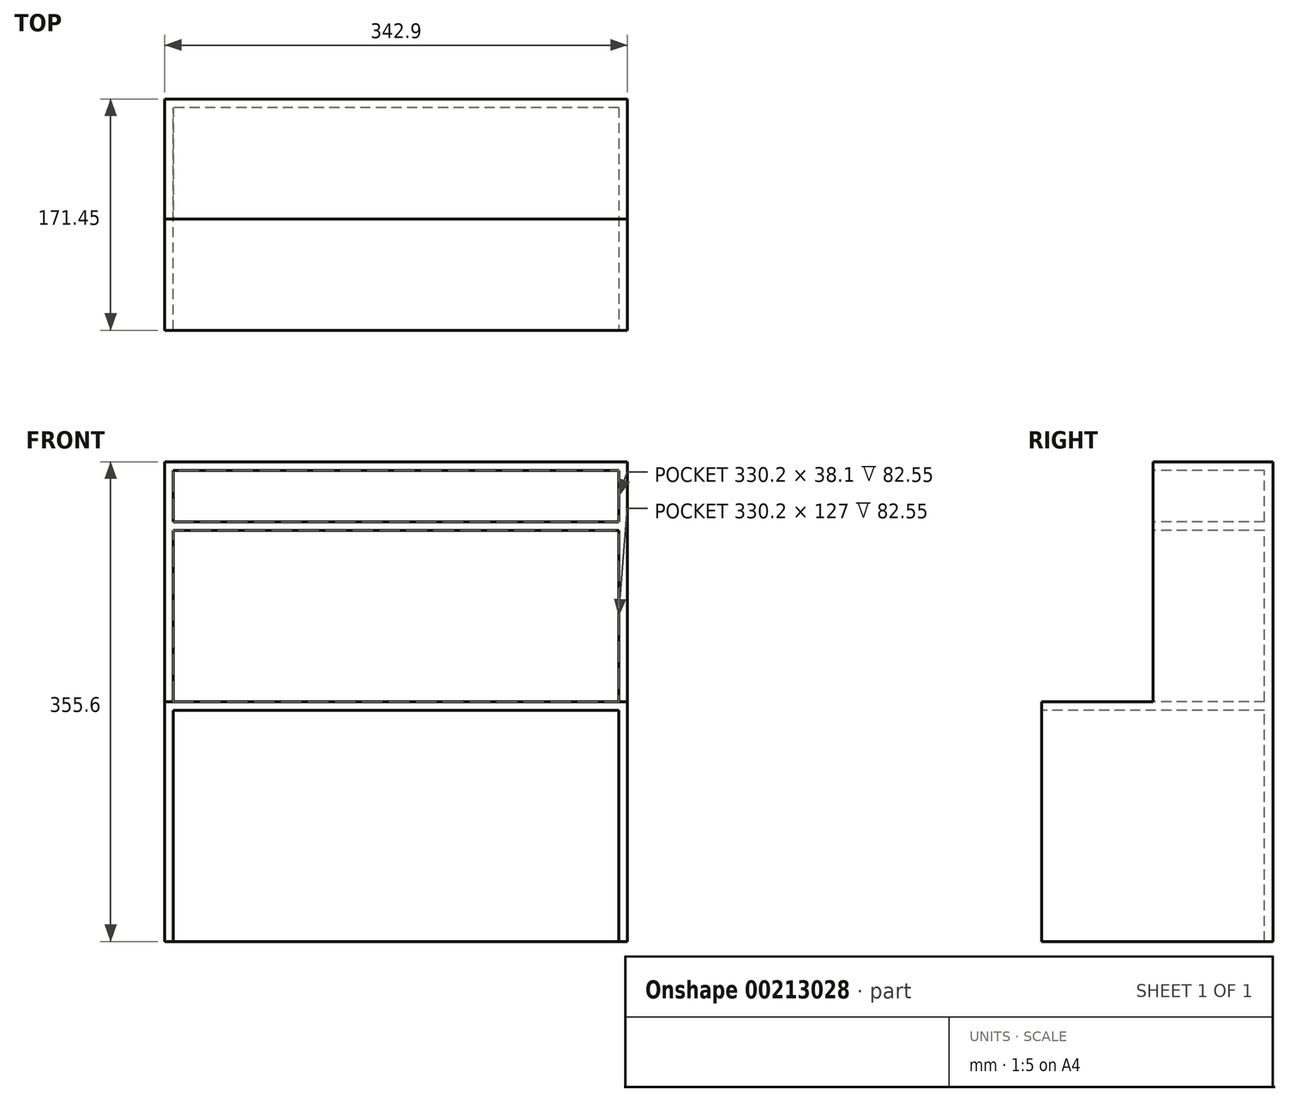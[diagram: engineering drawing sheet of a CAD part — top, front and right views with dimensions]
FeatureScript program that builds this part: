
annotation { "Feature Type Name" : "Feature", "Feature Type Description" : "" }
export const myFeature = defineFeature(function(context is Context, id is Id, definition is map)
    precondition{}
    {
        {
            var Q0;
            Q0=qCreatedBy(makeId("Right.planeOp"),FACE);
            cPlane(context, id + "F0", {"entities" : qUnion([Q0]), "cplaneType" : CPlaneType.OFFSET, "offset" : 165.1 * mm, "width" : 152.4 * mm, "height" : 152.4 * mm});
        }
        {
            var Q0;
            Q0=qCreatedBy(id+"F0.planeOp",FACE);
            var sketch = newSketch(context, id + "F1", { "sketchPlane" : qUnion([Q0])});
            skLineSegment(sketch, "E0.bottom", {"start": v(-82.55, 0) * mm, "end": v(82.55, 0) * mm});
            skLineSegment(sketch, "E0.top", {"start": v(-82.55, 177.8) * mm, "end": v(0, 177.8) * mm});
            skLineSegment(sketch, "E0.left", {"start": v(-82.55, 0) * mm, "end": v(-82.55, 177.8) * mm});
            skLineSegment(sketch, "E1", {"start": v(-82.55, 88.9) * mm, "end": v(0, 88.9) * mm, "construction": true});
            skLineSegment(sketch, "E2", {"start": v(0, 177.8) * mm, "end": v(0, 355.6) * mm});
            skPoint(sketch, "E2.endSnap0", {"position": v(0, 177.8) * mm});
            skLineSegment(sketch, "E3", {"start": v(0, 355.6) * mm, "end": v(82.55, 355.6) * mm});
            skLineSegment(sketch, "E4", {"start": v(82.55, 0) * mm, "end": v(82.55, 355.6) * mm});
            skLineSegment(sketch, "E5", {"start": v(0, 88.9) * mm, "end": v(82.55, 88.9) * mm, "construction": true});
            skSolve(sketch);
        }
        {
            var Q0;
            Q0=makeQuery(id+"F1.imprint","IMPRINT",FACE,{"disambiguationData":[TD([[makeQuery(id+"F1.imprint","IMPRINT",EDGE,{"derivedFrom":sQuery(id+"F1.wireOp",EDGE,"E0.bottom")}),1.0]])]});
            extrude(context, id + "F2", {"entities" : qUnion([Q0]), "depth" : 6.35 * mm});
        }
        {
            var Q0;
            Q0=makeQuery(id+"F2.opExtrude","SWEPT_FACE",FACE,{"disambiguationData":[OSD([sQuery(id+"F1.wireOp",EDGE,"E0.left")])]});
            var sketch = newSketch(context, id + "F3", { "sketchPlane" : qUnion([Q0])});
            skLineSegment(sketch, "E6.bottom", {"start": v(165.1, 177.8) * mm, "end": v(0, 177.8) * mm});
            skLineSegment(sketch, "E6.top", {"start": v(165.1, 171.45) * mm, "end": v(0, 171.45) * mm});
            skLineSegment(sketch, "E6.left", {"start": v(165.1, 177.8) * mm, "end": v(165.1, 171.45) * mm});
            skLineSegment(sketch, "E6.right", {"start": v(0, 177.8) * mm, "end": v(0, 171.45) * mm});
            skSolve(sketch);
        }
        {
            var Q0;
            Q0=makeQuery(id+"F3.imprint","IMPRINT",FACE,{"disambiguationData":[TD([[makeQuery(id+"F3.imprint","IMPRINT",EDGE,{"derivedFrom":sQuery(id+"F3.wireOp",EDGE,"E6.bottom")}),1.0]])]});
            var Q1;
            Q1=makeQuery(id+"F2.opExtrude","SWEPT_FACE",FACE,{"disambiguationData":[OSD([sQuery(id+"F1.wireOp",EDGE,"E4")])]});
            extrude(context, id + "F4", {"entities" : qUnion([Q0]), "operationType" : NewBodyOperationType.ADD, "endBound" : BoundingType.UP_TO_SURFACE, "oppositeDirection" : true, "endBoundEntityFace" : qUnion([Q1]), "depth" : 25.4 * mm});
        }
        {
            var Q0;
            Q0=makeQuery(id+"F2.opExtrude","SWEPT_FACE",FACE,{"disambiguationData":[OSD([sQuery(id+"F1.wireOp",EDGE,"E2")])]});
            var sketch = newSketch(context, id + "F5", { "sketchPlane" : qUnion([Q0])});
            skLineSegment(sketch, "E7.bottom", {"start": v(165.1, 355.6) * mm, "end": v(0, 355.6) * mm});
            skLineSegment(sketch, "E7.top", {"start": v(165.1, 349.25) * mm, "end": v(0, 349.25) * mm});
            skLineSegment(sketch, "E7.left", {"start": v(165.1, 355.6) * mm, "end": v(165.1, 349.25) * mm});
            skLineSegment(sketch, "E7.right", {"start": v(0, 355.6) * mm, "end": v(0, 349.25) * mm});
            skLineSegment(sketch, "E8.bottom", {"start": v(165.1, 311.15) * mm, "end": v(0, 311.15) * mm});
            skLineSegment(sketch, "E8.top", {"start": v(165.1, 304.8) * mm, "end": v(0, 304.8) * mm});
            skLineSegment(sketch, "E8.left", {"start": v(165.1, 311.15) * mm, "end": v(165.1, 304.8) * mm});
            skLineSegment(sketch, "E8.right", {"start": v(0, 311.15) * mm, "end": v(0, 304.8) * mm});
            skSolve(sketch);
        }
        {
            var Q0;
            Q0=makeQuery(id+"F5.imprint","IMPRINT",FACE,{"disambiguationData":[TD([[makeQuery(id+"F5.imprint","IMPRINT",EDGE,{"derivedFrom":sQuery(id+"F5.wireOp",EDGE,"E7.bottom")}),1.0]])]});
            var Q1;
            Q1=makeQuery(id+"F5.imprint","IMPRINT",FACE,{"disambiguationData":[TD([[makeQuery(id+"F5.imprint","IMPRINT",EDGE,{"derivedFrom":sQuery(id+"F5.wireOp",EDGE,"E8.bottom")}),1.0]])]});
            var Q2;
            {var subQ0=sQuery(id+"F1.wireOp",EDGE,"E4");Q2=makeQuery(id+"F4.boolean.opBoolean","MERGE",FACE,{"derivedFrom":[makeQuery(id+"F2.opExtrude","SWEPT_FACE",FACE,{"disambiguationData":[OSD([subQ0])]}),makeQuery(id+"F4.opExtrude","CAP_FACE",FACE,{"disambiguationData":[OSD([subQ0])],"isStart":false})]});}
            extrude(context, id + "F6", {"entities" : qUnion([Q0, Q1]), "operationType" : NewBodyOperationType.ADD, "endBound" : BoundingType.UP_TO_SURFACE, "oppositeDirection" : true, "endBoundEntityFace" : qUnion([Q2]), "depth" : 25.4 * mm});
        }
        {
            var Q0;
            Q0=makeQuery(id+"F2.opExtrude","SWEPT_BODY",BODY,{"disambiguationData":[OSD([sQuery(id+"F1.wireOp",EDGE,"E0.bottom"),sQuery(id+"F1.wireOp",EDGE,"E0.top"),sQuery(id+"F1.wireOp",EDGE,"E0.left"),sQuery(id+"F1.wireOp",EDGE,"E2"),sQuery(id+"F1.wireOp",EDGE,"E3"),sQuery(id+"F1.wireOp",EDGE,"E4")])]});
            var Q1;
            Q1=qCreatedBy(makeId("Right.planeOp"),FACE);
            mirror(context, id + "F7", {"operationType" : NewBodyOperationType.ADD, "entities" : qUnion([Q0]), "mirrorPlane" : qUnion([Q1])});
        }
        {
            var Q0;
            {var subQ0=sQuery(id+"F1.wireOp",EDGE,"E4");var subQ1=makeQuery(id+"F6.boolean.opBoolean","MERGE",FACE,{"derivedFrom":[makeQuery(id+"F4.boolean.opBoolean","MERGE",FACE,{"derivedFrom":[makeQuery(id+"F2.opExtrude","SWEPT_FACE",FACE,{"disambiguationData":[OSD([subQ0])]}),makeQuery(id+"F4.opExtrude","CAP_FACE",FACE,{"disambiguationData":[OSD([subQ0])],"isStart":false})]}),makeQuery(id+"F6.opExtrude","CAP_FACE",FACE,{"disambiguationData":[OSD([subQ0]),ownerDisambiguation([makeQuery(id+"F6.opExtrude","SWEPT_BODY",BODY,{"disambiguationData":[OSD([sQuery(id+"F5.wireOp",EDGE,"E7.bottom"),sQuery(id+"F5.wireOp",EDGE,"E7.top"),sQuery(id+"F5.wireOp",EDGE,"E7.left"),sQuery(id+"F5.wireOp",EDGE,"E7.right")])]})])],"isStart":false}),makeQuery(id+"F6.opExtrude","CAP_FACE",FACE,{"disambiguationData":[OSD([subQ0]),ownerDisambiguation([makeQuery(id+"F6.opExtrude","SWEPT_BODY",BODY,{"disambiguationData":[OSD([sQuery(id+"F5.wireOp",EDGE,"E8.bottom"),sQuery(id+"F5.wireOp",EDGE,"E8.top"),sQuery(id+"F5.wireOp",EDGE,"E8.left"),sQuery(id+"F5.wireOp",EDGE,"E8.right")])]})])],"isStart":false})]});Q0=makeQuery(id+"F7.boolean.opBoolean","MERGE",FACE,{"derivedFrom":[subQ1,makeQuery(id+"F7.opPattern","COPY",FACE,{"derivedFrom":subQ1,"instanceName":"1"})]});}
            var sketch = newSketch(context, id + "F8", { "sketchPlane" : qUnion([Q0])});
            skLineSegment(sketch, "E9.bottom", {"start": v(-171.45, 355.6) * mm, "end": v(171.45, 355.6) * mm});
            skLineSegment(sketch, "E9.top", {"start": v(-171.45, 0) * mm, "end": v(171.45, 0) * mm});
            skLineSegment(sketch, "E9.left", {"start": v(-171.45, 355.6) * mm, "end": v(-171.45, 0) * mm});
            skLineSegment(sketch, "E9.right", {"start": v(171.45, 355.6) * mm, "end": v(171.45, 0) * mm});
            skSolve(sketch);
        }
        {
            var Q0;
            Q0 = qSketchRegion(id + "F8", true);
            extrude(context, id + "F9", {"entities" : qUnion([Q0]), "operationType" : NewBodyOperationType.ADD, "depth" : 6.35 * mm});
        }
    });
